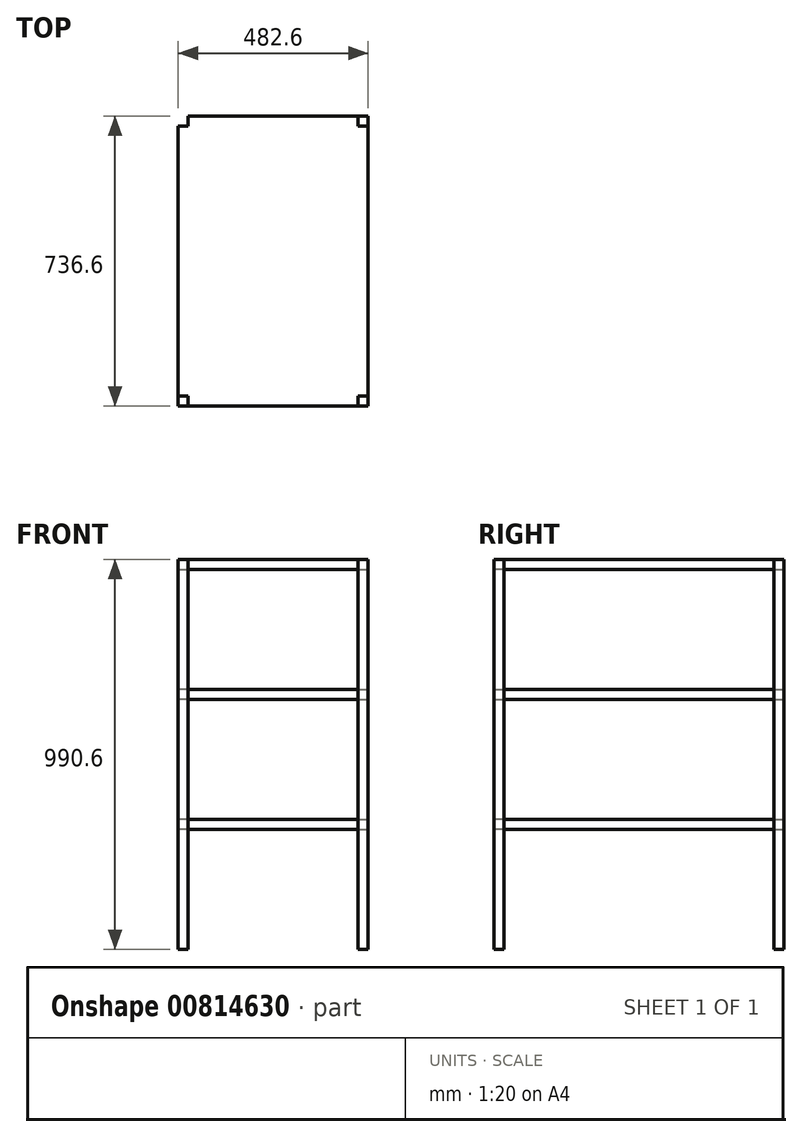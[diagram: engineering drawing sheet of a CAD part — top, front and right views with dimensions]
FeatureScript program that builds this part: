
annotation { "Feature Type Name" : "Feature", "Feature Type Description" : "" }
export const myFeature = defineFeature(function(context is Context, id is Id, definition is map)
    precondition{}
    {
        {
            var Q0;
            Q0=qCreatedBy(makeId("Top.planeOp"),FACE);
            var sketch = newSketch(context, id + "F0", { "sketchPlane" : qUnion([Q0])});
            skLineSegment(sketch, "E0.bottom", {"start": v(241.3, -368.3) * mm, "end": v(-241.3, -368.3) * mm});
            skLineSegment(sketch, "E0.top", {"start": v(241.3, 368.3) * mm, "end": v(-241.3, 368.3) * mm});
            skLineSegment(sketch, "E0.left", {"start": v(241.3, -368.3) * mm, "end": v(241.3, 368.3) * mm});
            skLineSegment(sketch, "E0.right", {"start": v(-241.3, -368.3) * mm, "end": v(-241.3, 368.3) * mm});
            skPoint(sketch, "E0.middle", {"position": v(0, 0) * mm});
            skLineSegment(sketch, "E1.bottom", {"start": v(-241.3, 368.3) * mm, "end": v(-215.9, 368.3) * mm});
            skLineSegment(sketch, "E1.top", {"start": v(-241.3, 342.9) * mm, "end": v(-215.9, 342.9) * mm});
            skLineSegment(sketch, "E1.left", {"start": v(-241.3, 368.3) * mm, "end": v(-241.3, 342.9) * mm});
            skLineSegment(sketch, "E1.right", {"start": v(-215.9, 368.3) * mm, "end": v(-215.9, 342.9) * mm});
            skLineSegment(sketch, "E2.MirrorCS", {"start": v(215.9, 368.3) * mm, "end": v(215.9, 342.9) * mm});
            skLineSegment(sketch, "E3.MirrorCS", {"start": v(241.3, 342.9) * mm, "end": v(215.9, 342.9) * mm});
            skLineSegment(sketch, "E4.MirrorCS", {"start": v(-215.9, -368.3) * mm, "end": v(-215.9, -342.9) * mm});
            skLineSegment(sketch, "E5.MirrorCS", {"start": v(-241.3, -342.9) * mm, "end": v(-215.9, -342.9) * mm});
            skLineSegment(sketch, "E6.MirrorCS", {"start": v(215.9, -368.3) * mm, "end": v(215.9, -342.9) * mm});
            skLineSegment(sketch, "E7.MirrorCS", {"start": v(241.3, -342.9) * mm, "end": v(215.9, -342.9) * mm});
            skSolve(sketch);
        }
        {
            var Q0;
            Q0=makeQuery(id+"F0.imprint","IMPRINT",FACE,{"disambiguationData":[TD([[makeQuery(id+"F0.imprint","IMPRINT",EDGE,{"derivedFrom":sQuery(id+"F0.wireOp",EDGE,"E1.bottom")}),-1.0]])]});
            var Q1;
            {var subQ3=sQuery(id+"F0.wireOp",EDGE,"E2.MirrorCS");Q1=makeQuery(id+"F0.imprint","IMPRINT",FACE,{"disambiguationData":[TD([[makeQuery(id+"F0.imprint","IMPRINT",EDGE,{"derivedFrom":subQ3}),1.0]])]});}
            var Q2;
            {var subQ3=sQuery(id+"F0.wireOp",EDGE,"E4.MirrorCS");Q2=makeQuery(id+"F0.imprint","IMPRINT",FACE,{"disambiguationData":[TD([[makeQuery(id+"F0.imprint","IMPRINT",EDGE,{"derivedFrom":subQ3}),1.0]])]});}
            var Q3;
            {var subQ3=sQuery(id+"F0.wireOp",EDGE,"E6.MirrorCS");Q3=makeQuery(id+"F0.imprint","IMPRINT",FACE,{"disambiguationData":[TD([[makeQuery(id+"F0.imprint","IMPRINT",EDGE,{"derivedFrom":subQ3}),-1.0]])]});}
            extrude(context, id + "F1", {"entities" : qUnion([Q0, Q1, Q2, Q3]), "depth" : 990.6 * mm, "offsetDistance" : 25.4 * mm});
        }
        {
            var Q0;
            {var subQ3=sQuery(id+"F0.wireOp",EDGE,"E1.top");Q0=makeQuery(id+"F0.imprint","IMPRINT",FACE,{"disambiguationData":[TD([[makeQuery(id+"F0.imprint","IMPRINT",EDGE,{"derivedFrom":subQ3}),-1.0]])]});}
            cPlane(context, id + "F2", {"entities" : qUnion([Q0]), "cplaneType" : CPlaneType.OFFSET, "offset" : 304.8 * mm, "width" : 152.4 * mm, "height" : 152.4 * mm});
        }
        {
            var Q0;
            Q0=qCreatedBy(id+"F2.planeOp",FACE);
            var sketch = newSketch(context, id + "F3", { "sketchPlane" : qUnion([Q0])});
            skLineSegment(sketch, "E8.0.0", {"start": v(241.3, -342.9) * mm, "end": v(241.3, 342.9) * mm});
            skLineSegment(sketch, "E8.0.1", {"start": v(241.3, 342.9) * mm, "end": v(215.9, 342.9) * mm});
            skLineSegment(sketch, "E8.0.2", {"start": v(215.9, 342.9) * mm, "end": v(215.9, 368.3) * mm});
            skLineSegment(sketch, "E8.0.3", {"start": v(215.9, 368.3) * mm, "end": v(-215.9, 368.3) * mm});
            skLineSegment(sketch, "E8.0.4", {"start": v(-215.9, 368.3) * mm, "end": v(-215.9, 342.9) * mm});
            skLineSegment(sketch, "E8.0.5", {"start": v(-215.9, 342.9) * mm, "end": v(-241.3, 342.9) * mm});
            skLineSegment(sketch, "E8.0.6", {"start": v(-241.3, 342.9) * mm, "end": v(-241.3, -342.9) * mm});
            skLineSegment(sketch, "E8.0.7", {"start": v(-241.3, -342.9) * mm, "end": v(-215.9, -342.9) * mm});
            skLineSegment(sketch, "E8.0.8", {"start": v(-215.9, -342.9) * mm, "end": v(-215.9, -368.3) * mm});
            skLineSegment(sketch, "E8.0.9", {"start": v(-215.9, -368.3) * mm, "end": v(215.9, -368.3) * mm});
            skLineSegment(sketch, "E8.0.10", {"start": v(215.9, -368.3) * mm, "end": v(215.9, -342.9) * mm});
            skLineSegment(sketch, "E8.0.11", {"start": v(215.9, -342.9) * mm, "end": v(241.3, -342.9) * mm});
            skSolve(sketch);
        }
        {
            var Q0;
            Q0=makeQuery(id+"F3.imprint","IMPRINT",FACE,{"disambiguationData":[TD([[makeQuery(id+"F3.imprint","IMPRINT",EDGE,{"derivedFrom":sQuery(id+"F3.wireOp",EDGE,"E8.0.0")}),1.0]])]});
            extrude(context, id + "F4", {"entities" : qUnion([Q0]), "depth" : 25.4 * mm, "offsetDistance" : 25.4 * mm});
        }
        {
            var Q0;
            Q0=qCreatedBy(id+"F2.planeOp",FACE);
            cPlane(context, id + "F5", {"entities" : qUnion([Q0]), "cplaneType" : CPlaneType.OFFSET, "offset" : 330.2 * mm, "width" : 152.4 * mm, "height" : 152.4 * mm});
        }
        {
            var Q0;
            Q0=qCreatedBy(id+"F5.planeOp",FACE);
            var sketch = newSketch(context, id + "F6", { "sketchPlane" : qUnion([Q0])});
            skLineSegment(sketch, "E9.0.0", {"start": v(215.9, -368.3) * mm, "end": v(215.9, -342.9) * mm});
            skLineSegment(sketch, "E9.0.1", {"start": v(215.9, -342.9) * mm, "end": v(241.3, -342.9) * mm});
            skLineSegment(sketch, "E9.0.2", {"start": v(241.3, -342.9) * mm, "end": v(241.3, 342.9) * mm});
            skLineSegment(sketch, "E9.0.3", {"start": v(241.3, 342.9) * mm, "end": v(215.9, 342.9) * mm});
            skLineSegment(sketch, "E9.0.4", {"start": v(215.9, 342.9) * mm, "end": v(215.9, 368.3) * mm});
            skLineSegment(sketch, "E9.0.5", {"start": v(215.9, 368.3) * mm, "end": v(-215.9, 368.3) * mm});
            skLineSegment(sketch, "E9.0.6", {"start": v(-215.9, 368.3) * mm, "end": v(-215.9, 342.9) * mm});
            skLineSegment(sketch, "E9.0.7", {"start": v(-215.9, 342.9) * mm, "end": v(-241.3, 342.9) * mm});
            skLineSegment(sketch, "E9.0.8", {"start": v(-241.3, 342.9) * mm, "end": v(-241.3, -342.9) * mm});
            skLineSegment(sketch, "E9.0.9", {"start": v(-241.3, -342.9) * mm, "end": v(-215.9, -342.9) * mm});
            skLineSegment(sketch, "E9.0.10", {"start": v(-215.9, -342.9) * mm, "end": v(-215.9, -368.3) * mm});
            skLineSegment(sketch, "E9.0.11", {"start": v(-215.9, -368.3) * mm, "end": v(215.9, -368.3) * mm});
            skSolve(sketch);
        }
        {
            var Q0;
            Q0=makeQuery(id+"F6.imprint","IMPRINT",FACE,{"disambiguationData":[TD([[makeQuery(id+"F6.imprint","IMPRINT",EDGE,{"derivedFrom":sQuery(id+"F6.wireOp",EDGE,"E9.0.0")}),1.0]])]});
            extrude(context, id + "F7", {"entities" : qUnion([Q0]), "depth" : 25.4 * mm, "offsetDistance" : 25.4 * mm});
        }
        {
            var Q0;
            Q0=qCreatedBy(id+"F5.planeOp",FACE);
            cPlane(context, id + "F8", {"entities" : qUnion([Q0]), "cplaneType" : CPlaneType.OFFSET, "offset" : 330.2 * mm, "width" : 152.4 * mm, "height" : 152.4 * mm});
        }
        {
            var Q0;
            Q0=qCreatedBy(id+"F8.planeOp",FACE);
            var sketch = newSketch(context, id + "F9", { "sketchPlane" : qUnion([Q0])});
            skLineSegment(sketch, "E10.0.0", {"start": v(-215.9, -342.9) * mm, "end": v(-215.9, -368.3) * mm});
            skLineSegment(sketch, "E10.0.1", {"start": v(-215.9, -368.3) * mm, "end": v(215.9, -368.3) * mm});
            skLineSegment(sketch, "E10.0.2", {"start": v(215.9, -368.3) * mm, "end": v(215.9, -342.9) * mm});
            skLineSegment(sketch, "E10.0.3", {"start": v(215.9, -342.9) * mm, "end": v(241.3, -342.9) * mm});
            skLineSegment(sketch, "E10.0.4", {"start": v(241.3, -342.9) * mm, "end": v(241.3, 342.9) * mm});
            skLineSegment(sketch, "E10.0.5", {"start": v(241.3, 342.9) * mm, "end": v(215.9, 342.9) * mm});
            skLineSegment(sketch, "E10.0.6", {"start": v(215.9, 342.9) * mm, "end": v(215.9, 368.3) * mm});
            skLineSegment(sketch, "E10.0.7", {"start": v(215.9, 368.3) * mm, "end": v(-215.9, 368.3) * mm});
            skLineSegment(sketch, "E10.0.8", {"start": v(-215.9, 368.3) * mm, "end": v(-215.9, 342.9) * mm});
            skLineSegment(sketch, "E10.0.9", {"start": v(-215.9, 342.9) * mm, "end": v(-241.3, 342.9) * mm});
            skLineSegment(sketch, "E10.0.10", {"start": v(-241.3, 342.9) * mm, "end": v(-241.3, -342.9) * mm});
            skLineSegment(sketch, "E10.0.11", {"start": v(-241.3, -342.9) * mm, "end": v(-215.9, -342.9) * mm});
            skSolve(sketch);
        }
        {
            var Q0;
            Q0=makeQuery(id+"F9.imprint","IMPRINT",FACE,{"disambiguationData":[TD([[makeQuery(id+"F9.imprint","IMPRINT",EDGE,{"derivedFrom":sQuery(id+"F9.wireOp",EDGE,"E10.0.0")}),1.0]])]});
            extrude(context, id + "F10", {"entities" : qUnion([Q0]), "depth" : 25.4 * mm, "offsetDistance" : 25.4 * mm});
        }
    });
